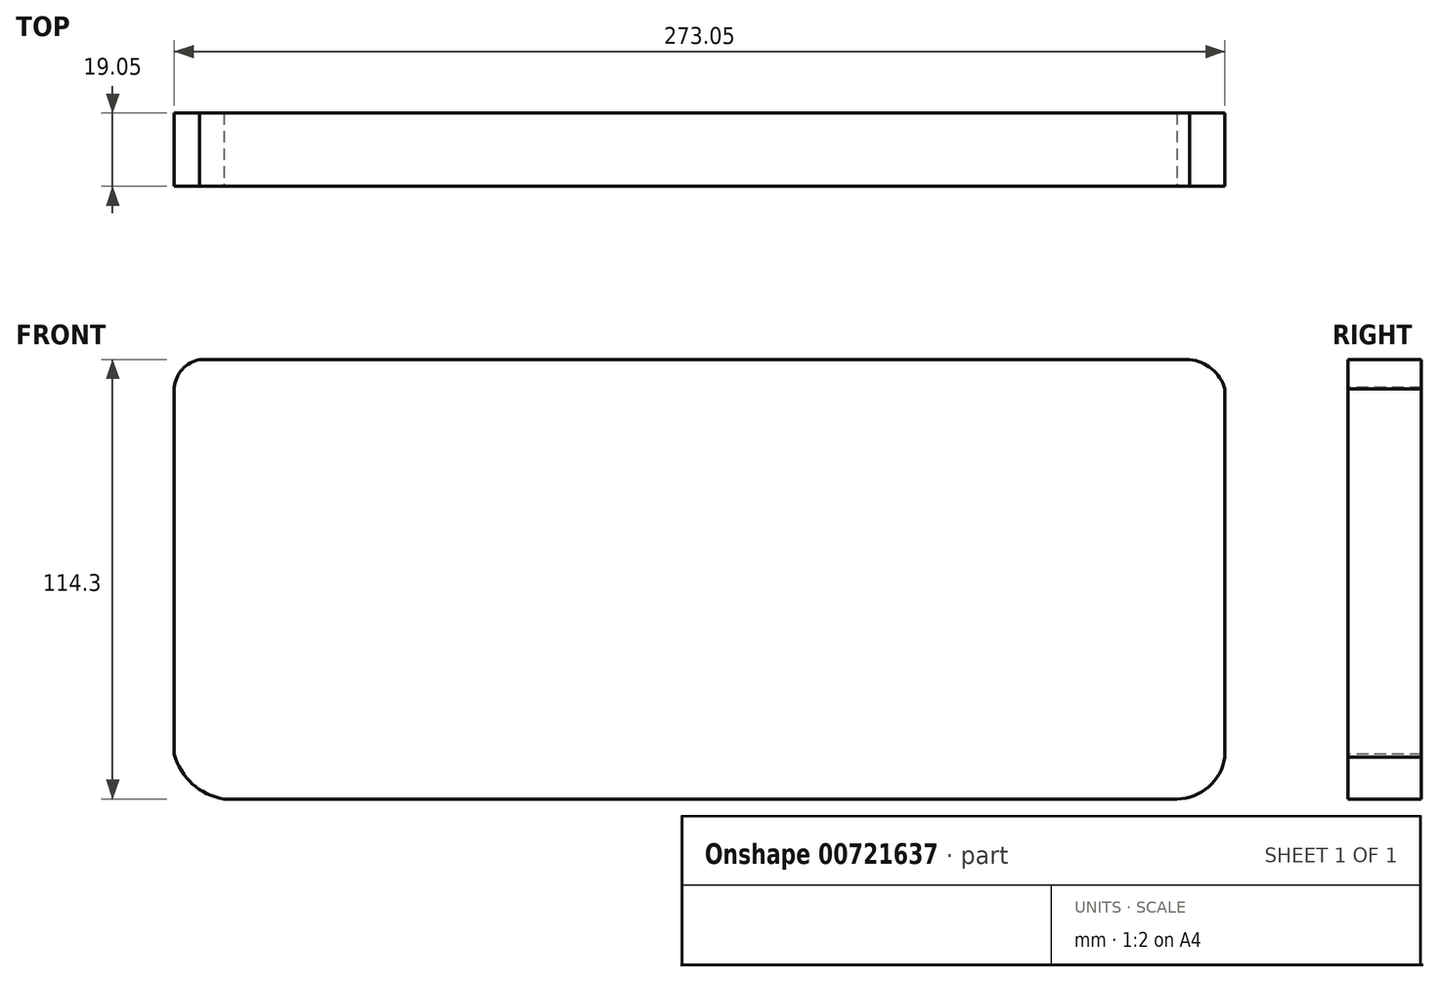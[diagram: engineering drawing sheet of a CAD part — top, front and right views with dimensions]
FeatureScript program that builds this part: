
annotation { "Feature Type Name" : "Feature", "Feature Type Description" : "" }
export const myFeature = defineFeature(function(context is Context, id is Id, definition is map)
    precondition{}
    {
        {
            var Q0;
            Q0=qCreatedBy(makeId("Front.planeOp"),FACE);
            var sketch = newSketch(context, id + "F0", { "sketchPlane" : qUnion([Q0])});
            skLineSegment(sketch, "E0.bottom", {"start": v(0, 0) * mm, "end": v(273.05, 0) * mm});
            skLineSegment(sketch, "E0.top", {"start": v(0, 114.3) * mm, "end": v(273.05, 114.3) * mm});
            skLineSegment(sketch, "E0.left", {"start": v(0, 0) * mm, "end": v(0, 114.3) * mm});
            skLineSegment(sketch, "E0.right", {"start": v(273.05, 0) * mm, "end": v(273.05, 114.3) * mm});
            skSolve(sketch);
        }
        {
            var Q0;
            Q0=makeQuery(id+"F0.imprint","IMPRINT",FACE,{"disambiguationData":[TD([[makeQuery(id+"F0.imprint","IMPRINT",EDGE,{"derivedFrom":sQuery(id+"F0.wireOp",EDGE,"E0.bottom")}),1.0]])]});
            extrude(context, id + "F1", {"entities" : qUnion([Q0]), "depth" : 19.05 * mm, "offsetDistance" : 25.4 * mm});
        }
        {
            var Q0;
            Q0=makeQuery(id+"F1.opExtrude","CAP_FACE",FACE,{"disambiguationData":[OSD([sQuery(id+"F0.wireOp",EDGE,"E0.bottom"),sQuery(id+"F0.wireOp",EDGE,"E0.top"),sQuery(id+"F0.wireOp",EDGE,"E0.left"),sQuery(id+"F0.wireOp",EDGE,"E0.right")])],"isStart":false});
            var sketch = newSketch(context, id + "F2", { "sketchPlane" : qUnion([Q0])});
            skArc(sketch, "E1", {"start": v(9.67, 114.3) * mm, "mid": v(2.65, 112.32) * mm, "end": v(0, 105.51) * mm});
            skArc(sketch, "E2", {"start": v(273.05, 106.7) * mm, "mid": v(269.6, 111.85) * mm, "end": v(263.9, 114.3) * mm});
            skArc(sketch, "E3", {"start": v(260.03, 0) * mm, "mid": v(268.58, 3.01) * mm, "end": v(273.05, 10.9) * mm});
            skArc(sketch, "E4", {"start": v(0, 11.67) * mm, "mid": v(4.72, 3.95) * mm, "end": v(12.87, 0) * mm});
            skSolve(sketch);
        }
        {
            var Q0;
            {var subQ0=sQuery(id+"F2.wireOp",EDGE,"E1");var subQ1=makeQuery(id+"F1.opExtrude","CAP_EDGE",EDGE,{"disambiguationData":[OSD([sQuery(id+"F0.wireOp",EDGE,"E0.top")])],"isStart":false});var subQ2=makeQuery(id+"F2.imprint","INTERSECT",VERTEX,{"disambiguationData":[OD(1.0)],"derivedFrom":[subQ1,subQ0]});Q0=makeQuery(id+"F2.imprint","IMPRINT",FACE,{"disambiguationData":[TD([[makeQuery(id+"F2.imprint","IMPRINT",EDGE,{"disambiguationData":[TD([[subQ2,-1.0]])],"derivedFrom":subQ0}),-1.0]])]});}
            var Q1;
            {var subQ0=sQuery(id+"F2.wireOp",EDGE,"E4");Q1=makeQuery(id+"F2.imprint","IMPRINT",FACE,{"disambiguationData":[TD([[makeQuery(id+"F2.imprint","IMPRINT",EDGE,{"derivedFrom":subQ0}),-1.0]])]});}
            var Q2;
            {var subQ0=sQuery(id+"F2.wireOp",EDGE,"E3");var subQ1=makeQuery(id+"F1.opExtrude","CAP_EDGE",EDGE,{"disambiguationData":[OSD([sQuery(id+"F0.wireOp",EDGE,"E0.right")])],"isStart":false});var subQ2=makeQuery(id+"F2.imprint","INTERSECT",VERTEX,{"derivedFrom":[subQ1,subQ0]});Q2=makeQuery(id+"F2.imprint","IMPRINT",FACE,{"disambiguationData":[TD([[makeQuery(id+"F2.imprint","IMPRINT",EDGE,{"disambiguationData":[TD([[subQ2,1.0]])],"derivedFrom":subQ0}),-1.0]])]});}
            var Q3;
            {var subQ0=sQuery(id+"F2.wireOp",EDGE,"E2");Q3=makeQuery(id+"F2.imprint","IMPRINT",FACE,{"disambiguationData":[TD([[makeQuery(id+"F2.imprint","IMPRINT",EDGE,{"derivedFrom":subQ0}),-1.0]])]});}
            extrude(context, id + "F3", {"entities" : qUnion([Q0, Q1, Q2, Q3]), "operationType" : NewBodyOperationType.REMOVE, "oppositeDirection" : true, "depth" : 25.4 * mm, "offsetDistance" : 25.4 * mm});
        }
    });
